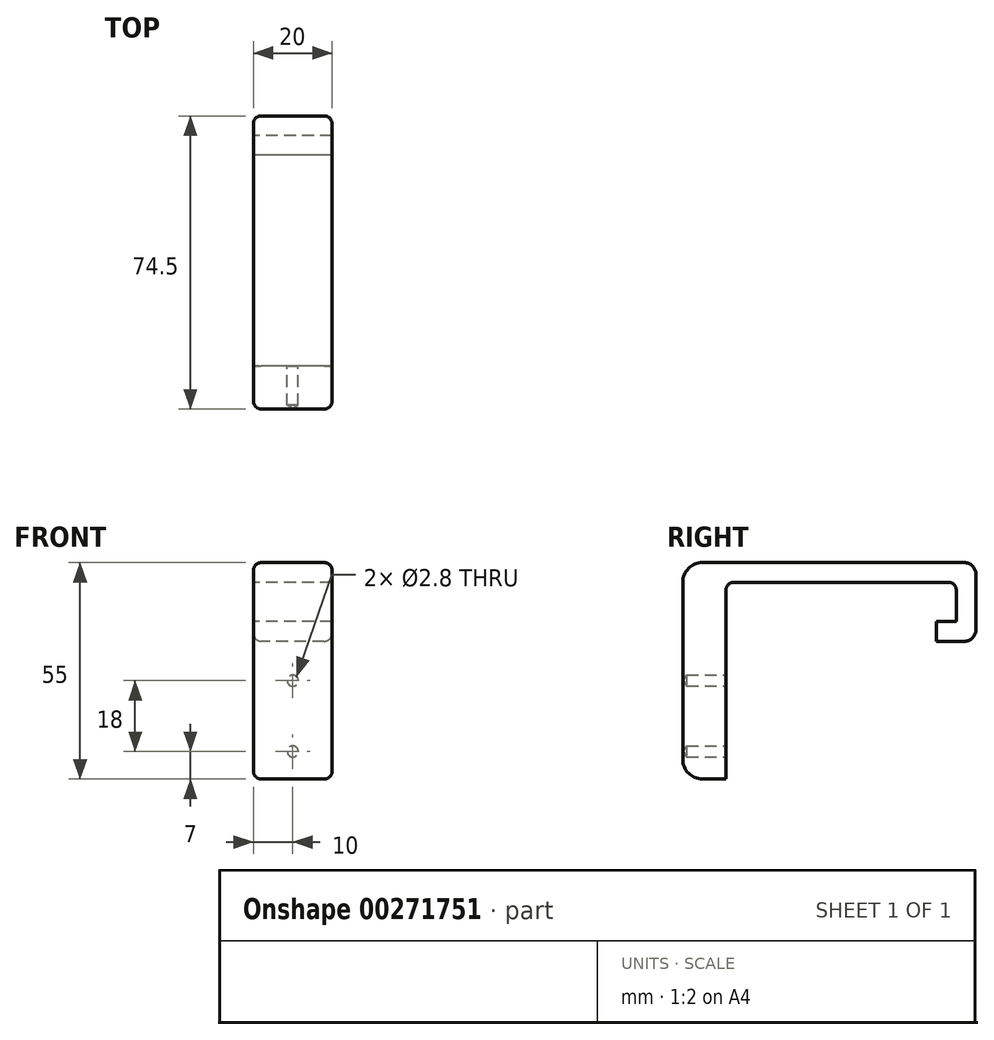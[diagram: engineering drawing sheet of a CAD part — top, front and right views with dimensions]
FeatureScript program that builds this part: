
annotation { "Feature Type Name" : "Feature", "Feature Type Description" : "" }
export const myFeature = defineFeature(function(context is Context, id is Id, definition is map)
    precondition{}
    {
        {
            var Q0;
            Q0=qCreatedBy(makeId("Right.planeOp"),FACE);
            var sketch = newSketch(context, id + "F0", { "sketchPlane" : qUnion([Q0])});
            skLineSegment(sketch, "E0", {"start": v(11.77, 0) * mm, "end": v(21.77, 0) * mm});
            skLineSegment(sketch, "E1", {"start": v(21.77, 0) * mm, "end": v(21.77, 20) * mm});
            skLineSegment(sketch, "E2", {"start": v(21.77, 20) * mm, "end": v(-52.73, 20) * mm});
            skLineSegment(sketch, "E3", {"start": v(-52.73, 20) * mm, "end": v(-52.73, -34.94) * mm});
            skLineSegment(sketch, "E4", {"start": v(-41.73, 15) * mm, "end": v(16.77, 15) * mm});
            skLineSegment(sketch, "E5", {"start": v(16.77, 15) * mm, "end": v(16.77, 5) * mm});
            skLineSegment(sketch, "E6", {"start": v(16.77, 5) * mm, "end": v(11.77, 5) * mm});
            skLineSegment(sketch, "E7", {"start": v(11.77, 5) * mm, "end": v(11.77, 0) * mm});
            skLineSegment(sketch, "E8", {"start": v(-41.73, -35) * mm, "end": v(-41.73, 15) * mm});
            skLineSegment(sketch, "E9", {"start": v(-52.73, -34.94) * mm, "end": v(-41.73, -35) * mm});
            skSolve(sketch);
        }
        {
            var Q0;
            Q0=qSketchRegion(id+"F0",true);
            extrude(context, id + "F1", {"entities" : qUnion([Q0]), "depth" : 20 * mm});
        }
        {
            var Q0;
            Q0=makeQuery(id+"F1.opExtrude","SWEPT_EDGE",EDGE,{"disambiguationData":[OSD([sQuery(id+"F0.wireOp",EDGE,"E1"),sQuery(id+"F0.wireOp",EDGE,"E2")])]});
            var Q1;
            Q1=makeQuery(id+"F1.opExtrude","SWEPT_EDGE",EDGE,{"disambiguationData":[OSD([sQuery(id+"F0.wireOp",EDGE,"E0"),sQuery(id+"F0.wireOp",EDGE,"E1")])]});
            fillet(context, id + "F2", {"entities" : qUnion([Q0, Q1]), "radius" : 3 * mm, "tangentPropagation" : true, "allowEdgeOverflow" : false});
        }
        {
            var Q0;
            Q0=makeQuery(id+"F1.opExtrude","SWEPT_EDGE",EDGE,{"disambiguationData":[OSD([sQuery(id+"F0.wireOp",EDGE,"E4"),sQuery(id+"F0.wireOp",EDGE,"E8")])]});
            var Q1;
            Q1=makeQuery(id+"F1.opExtrude","SWEPT_EDGE",EDGE,{"disambiguationData":[OSD([sQuery(id+"F0.wireOp",EDGE,"E4"),sQuery(id+"F0.wireOp",EDGE,"E5")])]});
            fillet(context, id + "F3", {"entities" : qUnion([Q0, Q1]), "radius" : 2 * mm, "tangentPropagation" : true, "allowEdgeOverflow" : false});
        }
        {
            var Q0;
            Q0=makeQuery(id+"F1.opExtrude","SWEPT_EDGE",EDGE,{"disambiguationData":[OSD([sQuery(id+"F0.wireOp",EDGE,"E3"),sQuery(id+"F0.wireOp",EDGE,"E9")])]});
            var Q1;
            Q1=makeQuery(id+"F1.opExtrude","SWEPT_EDGE",EDGE,{"disambiguationData":[OSD([sQuery(id+"F0.wireOp",EDGE,"E2"),sQuery(id+"F0.wireOp",EDGE,"E3")])]});
            fillet(context, id + "F4", {"entities" : qUnion([Q0, Q1]), "radius" : 5 * mm, "tangentPropagation" : true, "allowEdgeOverflow" : false});
        }
        {
            var Q0;
            Q0=makeQuery(id+"F1.opExtrude","SWEPT_FACE",FACE,{"disambiguationData":[OSD([sQuery(id+"F0.wireOp",EDGE,"E8")])]});
            var sketch = newSketch(context, id + "F5", { "sketchPlane" : qUnion([Q0])});
            skPoint(sketch, "E10", {"position": v(-10, -10) * mm});
            skPoint(sketch, "E11", {"position": v(-10, -28) * mm});
            skSolve(sketch);
        }
        {
            var Q0;
            Q0=sQuery(id+"F5.wireOp",VERTEX,"E11");
            var Q1;
            Q1=sQuery(id+"F5.wireOp",VERTEX,"E10");
            var Q2;
            Q2=makeQuery(id+"F1.opExtrude","SWEPT_BODY",BODY,{"disambiguationData":[OSD([sQuery(id+"F0.wireOp",EDGE,"E0"),sQuery(id+"F0.wireOp",EDGE,"E1"),sQuery(id+"F0.wireOp",EDGE,"E2"),sQuery(id+"F0.wireOp",EDGE,"E3"),sQuery(id+"F0.wireOp",EDGE,"E4"),sQuery(id+"F0.wireOp",EDGE,"E5"),sQuery(id+"F0.wireOp",EDGE,"E6"),sQuery(id+"F0.wireOp",EDGE,"E7"),sQuery(id+"F0.wireOp",EDGE,"E8"),sQuery(id+"F0.wireOp",EDGE,"E9")])]});
            hole(context, id + "F6", {"style" : HoleStyle.SIMPLE, "endStyle" : HoleEndStyle.BLIND, "holeDiameter" : 2.8 * mm, "holeDepth" : 10 * mm, "isTappedThrough" : true, "tappedDepth" : 12 * mm, "tapClearance" : 3, "startFromSketch" : true, "locations" : qUnion([Q0, Q1]), "scope" : qUnion([Q2])});
        }
        {
            var Q0;
            Q0=makeQuery(id+"F1.opExtrude","CAP_EDGE",EDGE,{"disambiguationData":[OSD([sQuery(id+"F0.wireOp",EDGE,"E3")])],"isStart":true});
            var Q1;
            Q1=makeQuery(id+"F1.opExtrude","CAP_EDGE",EDGE,{"disambiguationData":[OSD([sQuery(id+"F0.wireOp",EDGE,"E2")])],"isStart":false});
            fillet(context, id + "F7", {"entities" : qUnion([Q0, Q1]), "radius" : 2 * mm, "tangentPropagation" : true, "allowEdgeOverflow" : false});
        }
    });
